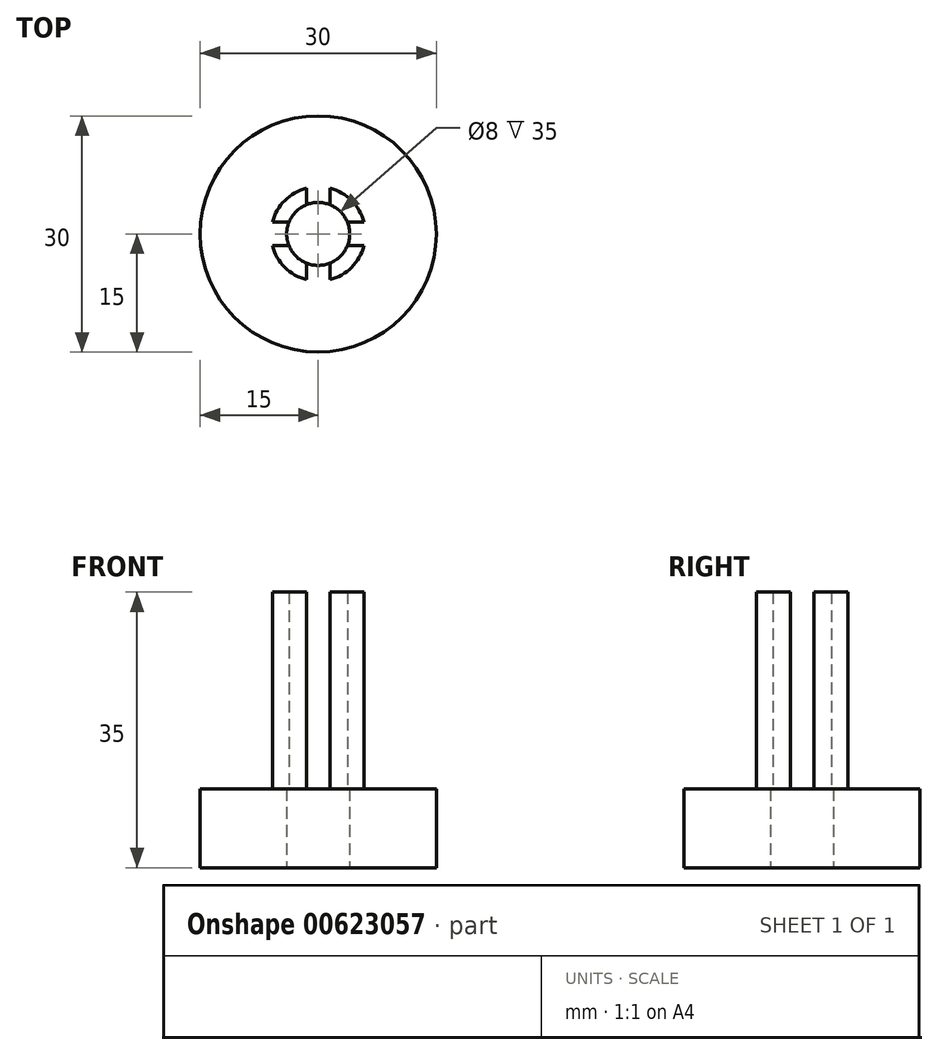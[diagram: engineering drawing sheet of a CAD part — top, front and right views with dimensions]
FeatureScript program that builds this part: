
annotation { "Feature Type Name" : "Feature", "Feature Type Description" : "" }
export const myFeature = defineFeature(function(context is Context, id is Id, definition is map)
    precondition{}
    {
        {
            var Q0;
            Q0=qCreatedBy(makeId("Front.planeOp"),FACE);
            var sketch = newSketch(context, id + "F0", { "sketchPlane" : qUnion([Q0])});
            skLineSegment(sketch, "E0", {"start": v(0, 0) * mm, "end": v(-15, 0) * mm});
            skLineSegment(sketch, "E1", {"start": v(-15, 0) * mm, "end": v(-15, 10) * mm});
            skLineSegment(sketch, "E2", {"start": v(-15, 10) * mm, "end": v(-6, 10) * mm});
            skLineSegment(sketch, "E3", {"start": v(-6, 10) * mm, "end": v(-6, 35) * mm});
            skLineSegment(sketch, "E4", {"start": v(-6, 35) * mm, "end": v(0, 35) * mm});
            skLineSegment(sketch, "E5", {"start": v(0, 0) * mm, "end": v(0, 35) * mm});
            skSolve(sketch);
        }
        {
            var Q0;
            Q0 = qSketchRegion(id + "F0", true);
            var Q1;
            Q1 = qConstructionFilter(qBodyType(qCreatedBy(id + "F0" ,EDGE), BodyType.WIRE), ConstructionObject.NO);
            var Q2;
            Q2=sQuery(id+"F0.wireOp",EDGE,"E5");
            revolve(context, id + "F1", {"entities" : qUnion([Q0]), "surfaceEntities" : qUnion([Q1]), "axis" : qUnion([Q2]), "revolveType" : RevolveType.FULL});
        }
        {
            var Q0;
            Q0=makeQuery(id+"F1.opRevolve","SWEPT_FACE",FACE,{"disambiguationData":[OSD([sQuery(id+"F0.wireOp",EDGE,"E0")])]});
            var sketch = newSketch(context, id + "F2", { "sketchPlane" : qUnion([Q0])});
            skPoint(sketch, "E6", {"position": v(0, 0) * mm});
            skSolve(sketch);
        }
        {
            var Q0;
            Q0=sQuery(id+"F2.wireOp",VERTEX,"E6");
            var Q1;
            Q1=makeQuery(id+"F1.opRevolve","SWEPT_BODY",BODY,{"disambiguationData":[OSD([sQuery(id+"F0.wireOp",EDGE,"E0"),sQuery(id+"F0.wireOp",EDGE,"E1"),sQuery(id+"F0.wireOp",EDGE,"E2"),sQuery(id+"F0.wireOp",EDGE,"E3"),sQuery(id+"F0.wireOp",EDGE,"E4"),sQuery(id+"F0.wireOp",EDGE,"E5")])]});
            hole(context, id + "F3", {"style" : HoleStyle.SIMPLE, "endStyle" : HoleEndStyle.THROUGH, "holeDiameter" : 8 * mm, "majorDiameter" : 3 * mm, "isTappedThrough" : true, "tappedDepth" : 5 * mm, "tapClearance" : 3, "locations" : qUnion([Q0]), "scope" : qUnion([Q1])});
        }
        {
            var Q0;
            Q0=qCreatedBy(makeId("Front.planeOp"),FACE);
            var sketch = newSketch(context, id + "F4", { "sketchPlane" : qUnion([Q0])});
            skLineSegment(sketch, "E7.bottom", {"start": v(0, 10) * mm, "end": v(-1.5, 10) * mm});
            skLineSegment(sketch, "E7.top", {"start": v(0, 35) * mm, "end": v(-1.5, 35) * mm});
            skLineSegment(sketch, "E7.left", {"start": v(0, 10) * mm, "end": v(0, 35) * mm, "construction": true});
            skLineSegment(sketch, "E7.right", {"start": v(-1.5, 10) * mm, "end": v(-1.5, 35) * mm});
            skLineSegment(sketch, "E8.MirrorCS", {"start": v(0, 10) * mm, "end": v(1.5, 10) * mm});
            skLineSegment(sketch, "E9.MirrorCS", {"start": v(1.5, 10) * mm, "end": v(1.5, 35) * mm});
            skLineSegment(sketch, "E10.MirrorCS", {"start": v(0, 35) * mm, "end": v(1.5, 35) * mm});
            skSolve(sketch);
        }
        {
            var Q0;
            Q0 = qSketchRegion(id + "F4", true);
            extrude(context, id + "F5", {"entities" : qUnion([Q0]), "operationType" : NewBodyOperationType.REMOVE, "endBound" : BoundingType.SYMMETRIC, "oppositeDirection" : true, "depth" : 25 * mm, "offsetDistance" : 25 * mm});
        }
        {
            var Q0;
            Q0=qCreatedBy(makeId("Right.planeOp"),FACE);
            var sketch = newSketch(context, id + "F6", { "sketchPlane" : qUnion([Q0])});
            skLineSegment(sketch, "E11.bottom", {"start": v(0, 10) * mm, "end": v(-1.5, 10) * mm});
            skLineSegment(sketch, "E11.top", {"start": v(0, 35.13) * mm, "end": v(-1.5, 35.13) * mm});
            skLineSegment(sketch, "E11.left", {"start": v(0, 10) * mm, "end": v(0, 35.13) * mm, "construction": true});
            skLineSegment(sketch, "E11.right", {"start": v(-1.5, 10) * mm, "end": v(-1.5, 35.13) * mm});
            skLineSegment(sketch, "E12.MirrorCS", {"start": v(0, 10) * mm, "end": v(1.5, 10) * mm});
            skLineSegment(sketch, "E13.MirrorCS", {"start": v(1.5, 10) * mm, "end": v(1.5, 35.13) * mm});
            skLineSegment(sketch, "E14.MirrorCS", {"start": v(0, 35.13) * mm, "end": v(1.5, 35.13) * mm});
            skSolve(sketch);
        }
        {
            var Q0;
            Q0 = qSketchRegion(id + "F6", true);
            extrude(context, id + "F7", {"entities" : qUnion([Q0]), "operationType" : NewBodyOperationType.REMOVE, "endBound" : BoundingType.SYMMETRIC, "oppositeDirection" : true, "depth" : 25 * mm, "offsetDistance" : 25 * mm});
        }
    });
